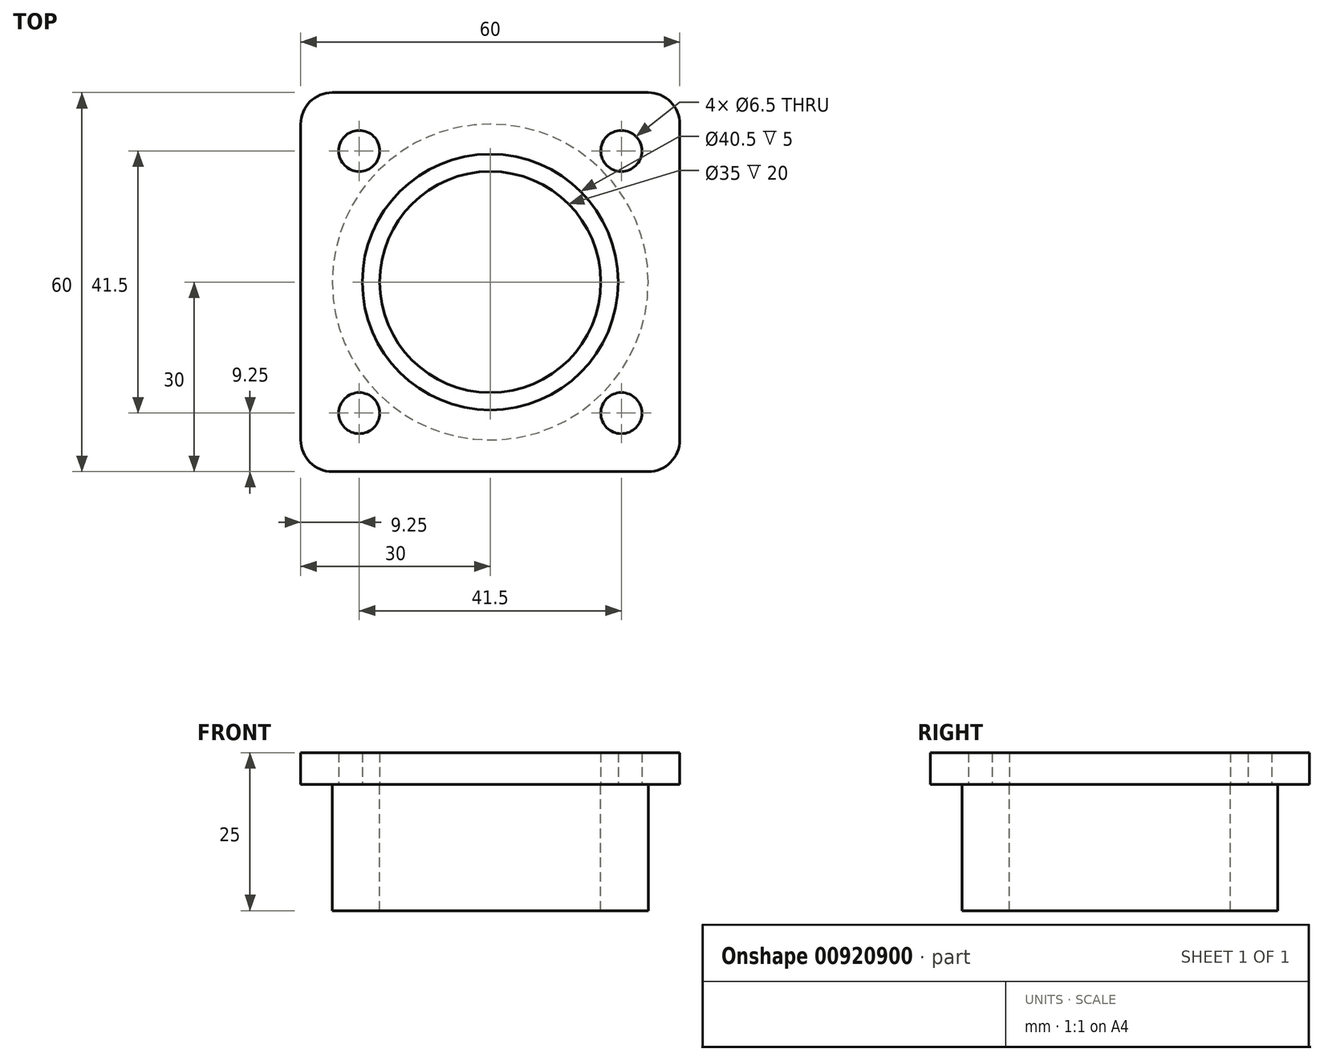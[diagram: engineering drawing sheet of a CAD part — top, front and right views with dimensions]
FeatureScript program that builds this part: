
annotation { "Feature Type Name" : "Feature", "Feature Type Description" : "" }
export const myFeature = defineFeature(function(context is Context, id is Id, definition is map)
    precondition{}
    {
        {
            var Q0;
            Q0=qCreatedBy(makeId("Top.planeOp"),FACE);
            var sketch = newSketch(context, id + "F0", { "sketchPlane" : qUnion([Q0])});
            skLineSegment(sketch, "E0.bottom", {"start": v(-30, 30) * mm, "end": v(30, 30) * mm});
            skLineSegment(sketch, "E0.top", {"start": v(-30, -30) * mm, "end": v(30, -30) * mm});
            skLineSegment(sketch, "E0.left", {"start": v(-30, 30) * mm, "end": v(-30, -30) * mm});
            skLineSegment(sketch, "E0.right", {"start": v(30, 30) * mm, "end": v(30, -30) * mm});
            skCircle(sketch, "E1", {"center": v(-20.75, 20.75) * mm, "radius": 3.25 * mm});
            skLineSegment(sketch, "E2", {"start": v(0, 46.31) * mm, "end": v(0, -34.79) * mm, "construction": true});
            skLineSegment(sketch, "E3", {"start": v(-39.4, 0) * mm, "end": v(37, 0) * mm, "construction": true});
            skCircle(sketch, "E4.MirrorC", {"center": v(20.75, 20.75) * mm, "radius": 3.25 * mm});
            skCircle(sketch, "E5.MirrorC", {"center": v(-20.75, -20.75) * mm, "radius": 3.25 * mm});
            skCircle(sketch, "E6.MirrorC", {"center": v(20.75, -20.75) * mm, "radius": 3.25 * mm});
            skCircle(sketch, "E7", {"center": v(0, 0) * mm, "radius": 20.25 * mm});
            skSolve(sketch);
        }
        {
            var Q0;
            Q0 = qSketchRegion(id + "F0", true);
            extrude(context, id + "F1", {"entities" : qUnion([Q0]), "depth" : 5 * mm, "offsetDistance" : 25 * mm});
        }
        {
            var Q0;
            Q0=makeQuery(id+"F1.opExtrude","SWEPT_EDGE",EDGE,{"disambiguationData":[OSD([sQuery(id+"F0.wireOp",EDGE,"E0.top"),sQuery(id+"F0.wireOp",EDGE,"E0.left")])]});
            var Q1;
            Q1=makeQuery(id+"F1.opExtrude","SWEPT_EDGE",EDGE,{"disambiguationData":[OSD([sQuery(id+"F0.wireOp",EDGE,"E0.top"),sQuery(id+"F0.wireOp",EDGE,"E0.right")])]});
            var Q2;
            Q2=makeQuery(id+"F1.opExtrude","SWEPT_EDGE",EDGE,{"disambiguationData":[OSD([sQuery(id+"F0.wireOp",EDGE,"E0.bottom"),sQuery(id+"F0.wireOp",EDGE,"E0.right")])]});
            var Q3;
            Q3=makeQuery(id+"F1.opExtrude","SWEPT_EDGE",EDGE,{"disambiguationData":[OSD([sQuery(id+"F0.wireOp",EDGE,"E0.bottom"),sQuery(id+"F0.wireOp",EDGE,"E0.left")])]});
            fillet(context, id + "F2", {"entities" : qUnion([Q0, Q1, Q2, Q3]), "radius" : 5 * mm, "tangentPropagation" : true, "allowEdgeOverflow" : false});
        }
        {
            var Q0;
            Q0=makeQuery(id+"F1.opExtrude","CAP_FACE",FACE,{"disambiguationData":[OSD([sQuery(id+"F0.wireOp",EDGE,"E0.bottom"),sQuery(id+"F0.wireOp",EDGE,"E0.top"),sQuery(id+"F0.wireOp",EDGE,"E0.left"),sQuery(id+"F0.wireOp",EDGE,"E0.right"),sQuery(id+"F0.wireOp",EDGE,"E1"),sQuery(id+"F0.wireOp",EDGE,"E4.MirrorC"),sQuery(id+"F0.wireOp",EDGE,"E5.MirrorC"),sQuery(id+"F0.wireOp",EDGE,"E6.MirrorC"),sQuery(id+"F0.wireOp",EDGE,"E7")])],"isStart":false});
            var sketch = newSketch(context, id + "F3", { "sketchPlane" : qUnion([Q0])});
            skCircle(sketch, "E8", {"center": v(0, 0) * mm, "radius": 19.5 * mm});
            skSolve(sketch);
        }
        {
            var Q0;
            Q0 = qSketchRegion(id + "F3", true);
            extrude(context, id + "F4", {"entities" : qUnion([Q0]), "operationType" : NewBodyOperationType.REMOVE, "oppositeDirection" : true, "depth" : 5 * mm, "offsetDistance" : 25 * mm});
        }
        {
            var Q0;
            Q0=makeQuery(id+"F1.opExtrude","CAP_FACE",FACE,{"disambiguationData":[OSD([sQuery(id+"F0.wireOp",EDGE,"E0.bottom"),sQuery(id+"F0.wireOp",EDGE,"E0.top"),sQuery(id+"F0.wireOp",EDGE,"E0.left"),sQuery(id+"F0.wireOp",EDGE,"E0.right"),sQuery(id+"F0.wireOp",EDGE,"E1"),sQuery(id+"F0.wireOp",EDGE,"E4.MirrorC"),sQuery(id+"F0.wireOp",EDGE,"E5.MirrorC"),sQuery(id+"F0.wireOp",EDGE,"E6.MirrorC"),sQuery(id+"F0.wireOp",EDGE,"E7")])],"isStart":true});
            var sketch = newSketch(context, id + "F5", { "sketchPlane" : qUnion([Q0])});
            skCircle(sketch, "E9", {"center": v(0, 0) * mm, "radius": 17.5 * mm});
            skCircle(sketch, "E10", {"center": v(0, 0) * mm, "radius": 25 * mm});
            skSolve(sketch);
        }
        {
            var Q0;
            Q0 = qSketchRegion(id + "F5", true);
            extrude(context, id + "F6", {"entities" : qUnion([Q0]), "operationType" : NewBodyOperationType.ADD, "depth" : 20 * mm, "offsetDistance" : 25 * mm});
        }
    });
